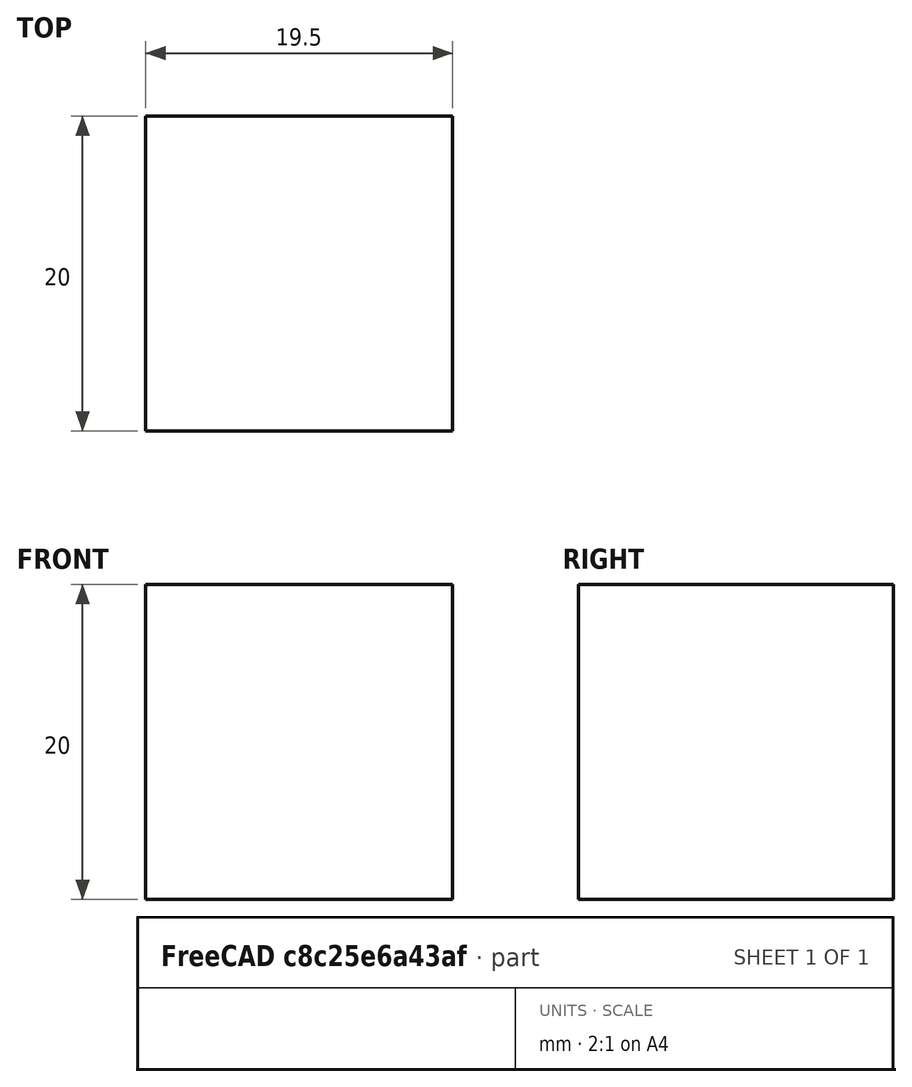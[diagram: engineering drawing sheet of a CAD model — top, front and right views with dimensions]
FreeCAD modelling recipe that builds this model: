
FCSTD DOCUMENT  (FreeCAD 0.19R24291 (Git))
Label: DIN-13
License: All rights reserved
LicenseURL: http://en.wikipedia.org/wiki/All_rights_reserved
objects: Sketcher::SketchObject×2, PartDesign::AdditiveBox×1, PartDesign::Body×1
note: 5 computed .brp shape members not serialized (recipe doc carries the construction recipe); baked Part::Feature solids carry a one-line shape summary decoded from their .brp

FEATURE [Sketcher::SketchObject] Sketch  label="Pins-sketch"
  FullyConstrained = false
  sketch-geometry (30):
    g0: Circle CenterX=-0.4 CenterY=6.5 CenterZ=0 NormalX=0 NormalY=0 NormalZ=1 AngleXU=0 Radius=0.505
    g1: Circle CenterX=-0.4 CenterY=6.5 CenterZ=0 NormalX=0 NormalY=0 NormalZ=1 AngleXU=0 Radius=0.5
    g2: Circle CenterX=-0.4 CenterY=2.5 CenterZ=0 NormalX=0 NormalY=0 NormalZ=1 AngleXU=0 Radius=0.505
    g3: Circle CenterX=-0.4 CenterY=2.5 CenterZ=0 NormalX=0 NormalY=0 NormalZ=1 AngleXU=0 Radius=0.5
    g4: Circle CenterX=-2.5 CenterY=-7.2 CenterZ=0 NormalX=0 NormalY=0 NormalZ=1 AngleXU=0 Radius=0.705
    g5: Circle CenterX=-2.5 CenterY=-7.2 CenterZ=0 NormalX=0 NormalY=0 NormalZ=1 AngleXU=0 Radius=0.7
    g6: Circle CenterX=2.5 CenterY=-7.2 CenterZ=0 NormalX=0 NormalY=0 NormalZ=1 AngleXU=0 Radius=0.705
    g7: Circle CenterX=2.5 CenterY=-7.2 CenterZ=0 NormalX=0 NormalY=0 NormalZ=1 AngleXU=0 Radius=0.7
    g8: Circle CenterX=3.3 CenterY=4.5 CenterZ=0 NormalX=0 NormalY=0 NormalZ=1 AngleXU=0 Radius=0.505
    g9: Circle CenterX=3.3 CenterY=4.5 CenterZ=0 NormalX=0 NormalY=0 NormalZ=1 AngleXU=0 Radius=0.5
    g10: Circle CenterX=0.8 CenterY=4.5 CenterZ=0 NormalX=0 NormalY=0 NormalZ=1 AngleXU=0 Radius=0.505
    g11: Circle CenterX=0.8 CenterY=4.5 CenterZ=0 NormalX=0 NormalY=0 NormalZ=1 AngleXU=0 Radius=0.5
    g12: Circle CenterX=0.8 CenterY=8.5 CenterZ=0 NormalX=0 NormalY=0 NormalZ=1 AngleXU=0 Radius=0.505
    g13: Circle CenterX=0.8 CenterY=8.5 CenterZ=0 NormalX=0 NormalY=0 NormalZ=1 AngleXU=0 Radius=0.5
    g14: Circle CenterX=-1.6 CenterY=8.5 CenterZ=0 NormalX=0 NormalY=0 NormalZ=1 AngleXU=0 Radius=0.505
    g15: Circle CenterX=-1.6 CenterY=8.5 CenterZ=0 NormalX=0 NormalY=0 NormalZ=1 AngleXU=0 Radius=0.5
    g16: Circle CenterX=3.3 CenterY=8.5 CenterZ=0 NormalX=0 NormalY=0 NormalZ=1 AngleXU=0 Radius=0.505
    g17: Circle CenterX=3.3 CenterY=8.5 CenterZ=0 NormalX=0 NormalY=0 NormalZ=1 AngleXU=0 Radius=0.5
    g18: Circle CenterX=-4 CenterY=8.5 CenterZ=0 NormalX=0 NormalY=0 NormalZ=1 AngleXU=0 Radius=0.505
    g19: Circle CenterX=-4 CenterY=8.5 CenterZ=0 NormalX=0 NormalY=0 NormalZ=1 AngleXU=0 Radius=0.5
    g20: Circle CenterX=-4 CenterY=4.5 CenterZ=0 NormalX=0 NormalY=0 NormalZ=1 AngleXU=0 Radius=0.505
    g21: Circle CenterX=-4 CenterY=4.5 CenterZ=0 NormalX=0 NormalY=0 NormalZ=1 AngleXU=0 Radius=0.5
    g22: Circle CenterX=-2.8 CenterY=6.5 CenterZ=0 NormalX=0 NormalY=0 NormalZ=1 AngleXU=0 Radius=0.505
    g23: Circle CenterX=-2.8 CenterY=6.5 CenterZ=0 NormalX=0 NormalY=0 NormalZ=1 AngleXU=0 Radius=0.5
    g24: Circle CenterX=2.1 CenterY=6.5 CenterZ=0 NormalX=0 NormalY=0 NormalZ=1 AngleXU=0 Radius=0.505
    g25: Circle CenterX=2.1 CenterY=6.5 CenterZ=0 NormalX=0 NormalY=0 NormalZ=1 AngleXU=0 Radius=0.5
    g26: Circle CenterX=4.5 CenterY=6.5 CenterZ=0 NormalX=0 NormalY=0 NormalZ=1 AngleXU=0 Radius=0.505
    g27: Circle CenterX=4.5 CenterY=6.5 CenterZ=0 NormalX=0 NormalY=0 NormalZ=1 AngleXU=0 Radius=0.5
    g28: Circle CenterX=-1.6 CenterY=4.5 CenterZ=0 NormalX=0 NormalY=0 NormalZ=1 AngleXU=0 Radius=0.505
    g29: Circle CenterX=-1.6 CenterY=4.5 CenterZ=0 NormalX=0 NormalY=0 NormalZ=1 AngleXU=0 Radius=0.5
FEATURE [Sketcher::SketchObject] Sketch001  label="Shell-sketch"
  FullyConstrained = false
  MapMode = 5
  Support = -> [XY_Plane]
  sketch-geometry (4):
    g0: LineSegment StartX=-9.75 StartY=-9.9365 StartZ=0 EndX=9.75 EndY=-9.9365 EndZ=0
    g1: LineSegment StartX=9.75 StartY=9.9365 StartZ=0 EndX=-9.75 EndY=9.9365 EndZ=0
    g2: LineSegment StartX=-9.6865 StartY=10 StartZ=0 EndX=-9.6865 EndY=-10 EndZ=0
    g3: LineSegment StartX=9.6865 StartY=-10 StartZ=0 EndX=9.6865 EndY=10 EndZ=0
FEATURE [PartDesign::AdditiveBox] Box
  AttacherType = Attacher::AttachEngine3D
  AttachmentOffset = pos=(-9.75,-10,0) rot=(0,0,1;0rad)
  Height = 20
  Length = 19.5
  MapMode = 5
  Placement = pos=(-9.75,-10,0) rot=(0,0,1;0rad)
  Support = -> [XY_Plane]
  Width = 20
FEATURE [PartDesign::Body] Body
  Group = -> [Sketch001,Box]
  Origin = -> Origin
  Tip = -> Box
